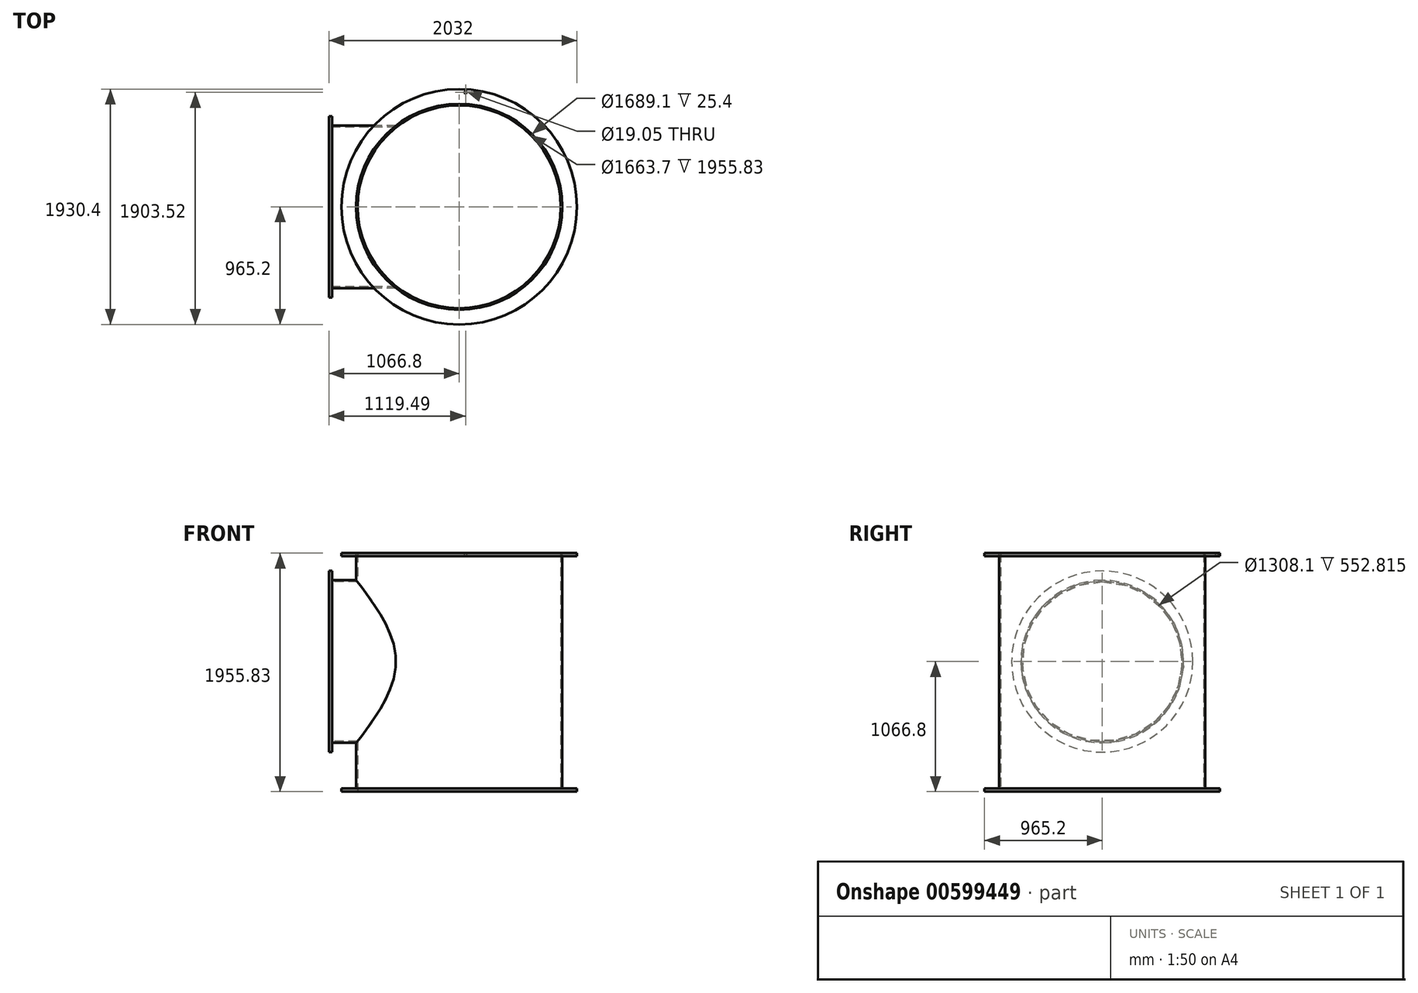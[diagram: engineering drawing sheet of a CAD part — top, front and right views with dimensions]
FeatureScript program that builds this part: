
annotation { "Feature Type Name" : "Feature", "Feature Type Description" : "" }
export const myFeature = defineFeature(function(context is Context, id is Id, definition is map)
    precondition{}
    {
        {
            var Q0;
            Q0=qCreatedBy(makeId("Top.planeOp"),FACE);
            var sketch = newSketch(context, id + "F0", { "sketchPlane" : qUnion([Q0])});
            skCircle(sketch, "E0", {"center": v(0, 0) * mm, "radius": 965.2 * mm});
            skCircle(sketch, "E1", {"center": v(0, 0) * mm, "radius": 844.55 * mm});
            skCircle(sketch, "E2", {"center": v(0, 0) * mm, "radius": 831.85 * mm});
            skSolve(sketch);
        }
        {
            var Q0;
            Q0=qSketchRegion(id+"F0",true);
            extrude(context, id + "F1", {"entities" : qUnion([Q0]), "depth" : 25.4 * mm});
        }
        {
            var Q0;
            Q0=makeQuery(id+"F0.imprint","IMPRINT",FACE,{"disambiguationData":[TD([[makeQuery(id+"F0.imprint","IMPRINT",EDGE,{"derivedFrom":sQuery(id+"F0.wireOp",EDGE,"E1")}),1.0]])]});
            extrude(context, id + "F2", {"entities" : qUnion([Q0]), "operationType" : NewBodyOperationType.ADD, "depth" : 1828.8 * mm + 127 * mm + 7 / 203.2 * mm});
        }
        {
            var Q0;
            Q0=makeQuery(id+"F2.opExtrude","CAP_FACE",FACE,{"disambiguationData":[OSD([sQuery(id+"F0.wireOp",EDGE,"E1"),sQuery(id+"F0.wireOp",EDGE,"E2")])],"isStart":false});
            var sketch = newSketch(context, id + "F3", { "sketchPlane" : qUnion([Q0])});
            skCircle(sketch, "E3", {"center": v(0, 0) * mm, "radius": 965.2 * mm});
            skCircle(sketch, "E4", {"center": v(0, 0) * mm, "radius": 844.55 * mm});
            skCircle(sketch, "E5", {"center": v(0, 0) * mm, "radius": 939.8 * mm, "construction": true});
            skLineSegment(sketch, "E6", {"start": v(0, 0) * mm, "end": v(0, 1081.52) * mm, "construction": true});
            skLineSegment(sketch, "E7", {"start": v(0, 0) * mm, "end": v(60.76, 1081.92) * mm, "construction": true});
            skPoint(sketch, "E8", {"position": v(52.7, 938.32) * mm});
            skSolve(sketch);
        }
        {
            var Q0;
            Q0=makeQuery(id+"F3.imprint","IMPRINT",FACE,{"disambiguationData":[TD([[makeQuery(id+"F3.imprint","IMPRINT",EDGE,{"derivedFrom":sQuery(id+"F3.wireOp",EDGE,"E3")}),1.0]])]});
            extrude(context, id + "F4", {"entities" : qUnion([Q0]), "oppositeDirection" : true, "depth" : 25.4 * mm});
        }
        {
            var Q0;
            Q0=sQuery(id+"F3.wireOp",VERTEX,"E8");
            var Q1;
            Q1=makeQuery(id+"F4.opExtrude","SWEPT_BODY",BODY,{"disambiguationData":[OSD([sQuery(id+"F3.wireOp",EDGE,"E3"),sQuery(id+"F3.wireOp",EDGE,"E4")])]});
            hole(context, id + "F5", {"style" : HoleStyle.SIMPLE, "endStyle" : HoleEndStyle.THROUGH, "holeDiameter" : 19.05 * mm, "isTappedThrough" : true, "tappedDepth" : 12.7 * mm, "tapClearance" : 3, "startFromSketch" : true, "locations" : qUnion([Q0]), "scope" : qUnion([Q1])});
        }
        {
            var Q0;
            Q0=qCreatedBy(makeId("Right.planeOp"),FACE);
            cPlane(context, id + "F6", {"entities" : qUnion([Q0]), "cplaneType" : CPlaneType.OFFSET, "offset" : 1066.8 * mm, "oppositeDirection" : true, "width" : 152.4 * mm, "height" : 152.4 * mm});
        }
        {
            var Q0;
            Q0=qCreatedBy(id+"F6.planeOp",FACE);
            var sketch = newSketch(context, id + "F7", { "sketchPlane" : qUnion([Q0])});
            skLineSegment(sketch, "E9", {"start": v(0, 0) * mm, "end": v(0, 1066.8) * mm, "construction": true});
            skCircle(sketch, "E10", {"center": v(0, 1066.8) * mm, "radius": 742.95 * mm});
            skCircle(sketch, "E11", {"center": v(0, 1066.8) * mm, "radius": 717.55 * mm, "construction": true});
            skCircle(sketch, "E12", {"center": v(0, 1066.8) * mm, "radius": 666.75 * mm});
            skCircle(sketch, "E13", {"center": v(0, 1066.8) * mm, "radius": 654.05 * mm});
            skSolve(sketch);
        }
        {
            var Q0;
            Q0=makeQuery(id+"F7.imprint","IMPRINT",FACE,{"disambiguationData":[TD([[makeQuery(id+"F7.imprint","IMPRINT",EDGE,{"derivedFrom":sQuery(id+"F7.wireOp",EDGE,"E10")}),1.0]])]});
            extrude(context, id + "F8", {"entities" : qUnion([Q0]), "depth" : 25.4 * mm});
        }
        {
            var Q0;
            Q0=makeQuery(id+"F7.imprint","IMPRINT",FACE,{"disambiguationData":[TD([[makeQuery(id+"F7.imprint","IMPRINT",EDGE,{"derivedFrom":sQuery(id+"F7.wireOp",EDGE,"E12")}),1.0]])]});
            var Q1;
            Q1=makeQuery(id+"F1.opExtrude","SWEPT_BODY",BODY,{"disambiguationData":[OSD([sQuery(id+"F0.wireOp",EDGE,"E0"),sQuery(id+"F0.wireOp",EDGE,"E1")])]});
            extrude(context, id + "F9", {"entities" : qUnion([Q0]), "operationType" : NewBodyOperationType.ADD, "endBound" : BoundingType.UP_TO_BODY, "endBoundEntityBody" : qUnion([Q1]), "depth" : 640.08 * mm});
        }
        {
            var Q0;
            Q0=makeQuery(id+"F7.imprint","IMPRINT",FACE,{"disambiguationData":[TD([[makeQuery(id+"F7.imprint","IMPRINT",EDGE,{"derivedFrom":sQuery(id+"F7.wireOp",EDGE,"E13")}),1.0]])]});
            extrude(context, id + "F10", {"entities" : qUnion([Q0]), "operationType" : NewBodyOperationType.REMOVE, "depth" : 784.86 * mm});
        }
    });
